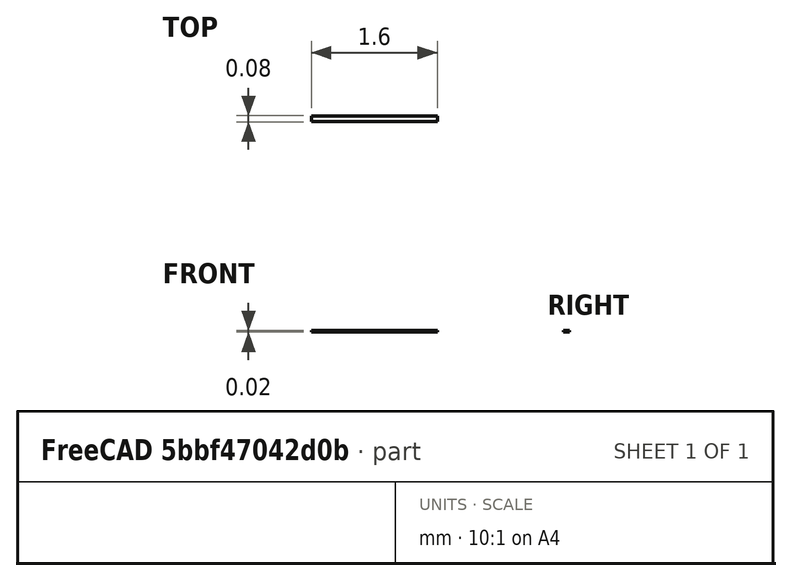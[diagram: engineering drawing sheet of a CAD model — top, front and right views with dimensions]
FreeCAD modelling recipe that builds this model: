
FCSTD DOCUMENT  (FreeCAD 0.17R12607 (Git))
Label: 1616 RGB LED Cathode
License: CreativeCommons Attribution-ShareAlike
LicenseURL: http://creativecommons.org/licenses/by-sa/4.0/
objects: Sketcher::SketchObject×1, PartDesign::Pad×1, PartDesign::Body×1
note: 4 computed .brp shape members not serialized (recipe doc carries the construction recipe); baked Part::Feature solids carry a one-line shape summary decoded from their .brp

FEATURE [Sketcher::SketchObject] Sketch
  MapMode = 5
  Support = -> [XY_Plane]
  sketch-geometry (4):
    g0: LineSegment StartX=-0.8 StartY=0.035 StartZ=0 EndX=0.8 EndY=0.035 EndZ=0
    g1: LineSegment StartX=0.8 StartY=0.035 StartZ=0 EndX=0.8 EndY=-0.035 EndZ=0
    g2: LineSegment StartX=0.8 StartY=-0.035 StartZ=0 EndX=-0.8 EndY=-0.035 EndZ=0
    g3: LineSegment StartX=-0.8 StartY=-0.035 StartZ=0 EndX=-0.8 EndY=0.035 EndZ=0
  constraints (12):
    c: Coincident(g0,g1)
    c: Coincident(g1,g2)
    c: Coincident(g2,g3)
    c: Coincident(g3,g0)
    c: Horizontal(g0)
    c: Horizontal(g2)
    c: Vertical(g1)
    c: Vertical(g3)
    c: Symmetric(g0,g0,g-2)
    c: Symmetric(g0,g1,g-1)
    c: DistanceX(g0,g0) = 1.6
    c: DistanceY(g1,g1) = 0.07
FEATURE [PartDesign::Pad] Pad
  Length = 0.02
  Length2 = 100
  Profile = -> Sketch
  Type = 0
FEATURE [PartDesign::Body] Body
  Group = -> [Sketch,Pad]
  Origin = -> Origin
  Tip = -> Pad
